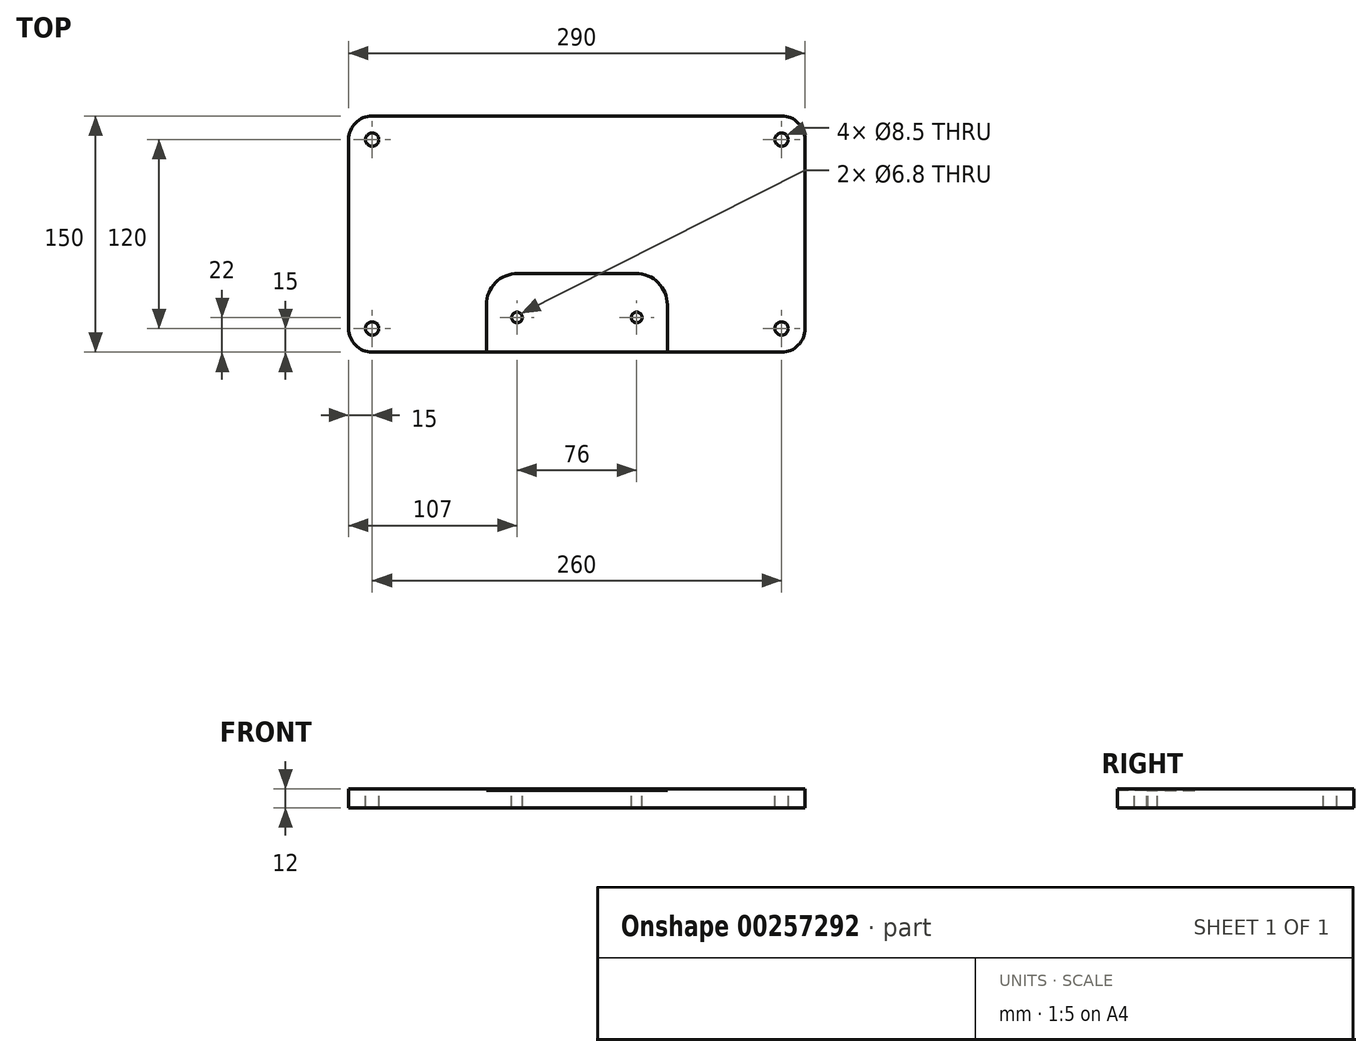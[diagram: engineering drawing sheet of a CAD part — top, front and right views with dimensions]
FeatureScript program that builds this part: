
annotation { "Feature Type Name" : "Feature", "Feature Type Description" : "" }
export const myFeature = defineFeature(function(context is Context, id is Id, definition is map)
    precondition{}
    {
        {
            var Q0;
            Q0=qCreatedBy(makeId("Top.planeOp"),FACE);
            var sketch = newSketch(context, id + "F0", { "sketchPlane" : qUnion([Q0])});
            skLineSegment(sketch, "E0", {"start": v(145, 150) * mm, "end": v(145, 0) * mm});
            skLineSegment(sketch, "E1", {"start": v(145, 150) * mm, "end": v(-145, 150) * mm});
            skLineSegment(sketch, "E2.MirrorCS", {"start": v(-145, 150) * mm, "end": v(-145, 0) * mm});
            skLineSegment(sketch, "E3", {"start": v(-145, 0) * mm, "end": v(145, 0) * mm});
            skSolve(sketch);
        }
        {
            var Q0;
            Q0=makeQuery(id+"F0.imprint","IMPRINT",FACE,{"disambiguationData":[TD([[makeQuery(id+"F0.imprint","IMPRINT",EDGE,{"derivedFrom":sQuery(id+"F0.wireOp",EDGE,"E0")}),-1.0]])]});
            extrude(context, id + "F1", {"entities" : qUnion([Q0]), "oppositeDirection" : true, "depth" : 12 * mm});
        }
        {
            var Q0;
            Q0=makeQuery(id+"F1.opExtrude","SWEPT_EDGE",EDGE,{"disambiguationData":[OSD([sQuery(id+"F0.wireOp",EDGE,"E1"),sQuery(id+"F0.wireOp",EDGE,"E2.MirrorCS")])]});
            var Q1;
            Q1=makeQuery(id+"F1.opExtrude","SWEPT_EDGE",EDGE,{"disambiguationData":[OSD([sQuery(id+"F0.wireOp",EDGE,"E2.MirrorCS"),sQuery(id+"F0.wireOp",EDGE,"E3")])]});
            var Q2;
            Q2=makeQuery(id+"F1.opExtrude","SWEPT_EDGE",EDGE,{"disambiguationData":[OSD([sQuery(id+"F0.wireOp",EDGE,"E0"),sQuery(id+"F0.wireOp",EDGE,"E1")])]});
            var Q3;
            Q3=makeQuery(id+"F1.opExtrude","SWEPT_EDGE",EDGE,{"disambiguationData":[OSD([sQuery(id+"F0.wireOp",EDGE,"E0"),sQuery(id+"F0.wireOp",EDGE,"E3")])]});
            fillet(context, id + "F2", {"entities" : qUnion([Q0, Q1, Q2, Q3]), "radius" : 15 * mm, "tangentPropagation" : true, "allowEdgeOverflow" : false});
        }
        {
            var Q0;
            Q0=makeQuery(id+"F1.opExtrude","CAP_FACE",FACE,{"disambiguationData":[OSD([sQuery(id+"F0.wireOp",EDGE,"E0"),sQuery(id+"F0.wireOp",EDGE,"E1"),sQuery(id+"F0.wireOp",EDGE,"E2.MirrorCS"),sQuery(id+"F0.wireOp",EDGE,"E3")])],"isStart":true});
            var sketch = newSketch(context, id + "F3", { "sketchPlane" : qUnion([Q0])});
            skPoint(sketch, "E4", {"position": v(130, 135) * mm});
            skPoint(sketch, "E5", {"position": v(130, 15) * mm});
            skPoint(sketch, "E6.MirrorP", {"position": v(-130, 135) * mm});
            skPoint(sketch, "E7.MirrorP", {"position": v(-130, 15) * mm});
            skLineSegment(sketch, "E8", {"start": v(57.5, 30) * mm, "end": v(57.5, -8) * mm});
            skLineSegment(sketch, "E9.MirrorCS", {"start": v(-57.5, 30) * mm, "end": v(-57.5, -8) * mm});
            skLineSegment(sketch, "E10", {"start": v(-37.5, 50) * mm, "end": v(37.5, 50) * mm});
            skLineSegment(sketch, "E11", {"start": v(-57.5, -8) * mm, "end": v(57.5, -8) * mm});
            skPoint(sketch, "E12.visualSharp", {"position": v(-57.5, 50) * mm});
            skArc(sketch, "E12.filletArc", {"start": v(-37.5, 50) * mm, "mid": v(-51.64, 44.14) * mm, "end": v(-57.5, 30) * mm});
            skPoint(sketch, "E13.visualSharp", {"position": v(57.5, 50) * mm});
            skArc(sketch, "E13.filletArc", {"start": v(57.5, 30) * mm, "mid": v(51.64, 44.14) * mm, "end": v(37.5, 50) * mm});
            skLineSegment(sketch, "E14", {"start": v(-47.11, 22) * mm, "end": v(45.69, 22) * mm, "construction": true});
            skPoint(sketch, "E15", {"position": v(38, 22) * mm});
            skPoint(sketch, "E16.MirrorP", {"position": v(-38, 22) * mm});
            skSolve(sketch);
        }
        {
            var Q0;
            Q0=sQuery(id+"F3.wireOp",VERTEX,"E4");
            var Q1;
            Q1=sQuery(id+"F3.wireOp",VERTEX,"E5");
            var Q2;
            Q2=sQuery(id+"F3.wireOp",VERTEX,"E6.MirrorP");
            var Q3;
            Q3=sQuery(id+"F3.wireOp",VERTEX,"E7.MirrorP");
            var Q4;
            Q4=makeQuery(id+"F1.opExtrude","SWEPT_BODY",BODY,{"disambiguationData":[OSD([sQuery(id+"F0.wireOp",EDGE,"E0"),sQuery(id+"F0.wireOp",EDGE,"E1"),sQuery(id+"F0.wireOp",EDGE,"E2.MirrorCS"),sQuery(id+"F0.wireOp",EDGE,"E3")])]});
            hole(context, id + "F4", {"style" : HoleStyle.SIMPLE, "endStyle" : HoleEndStyle.THROUGH, "standardTappedOrClearance" : lookupTablePath({ "standard" : "ISO", "fit" : "Normal", "engagement" : "75%", "pitch" : "1.5 mm", "size" : "M10", "type" : "Tapped" }), "standardBlindInLast" : lookupTablePath({ "fit" : "Standard", "standard" : "ISO", "engagement" : "75%", "pitch" : "1.5 mm", "size" : "M10", "type" : "Tapped" }), "holeDiameter" : 8.5 * mm, "showTappedDepth" : true, "tappedDepth" : 12 * mm, "tapClearance" : 3, "locations" : qUnion([Q0, Q1, Q2, Q3]), "scope" : qUnion([Q4]), "majorDiameter" : 10 * mm});
        }
        {
            var Q0;
            {var subQ0=sQuery(id+"F3.wireOp",EDGE,"E11");Q0=makeQuery(id+"F3.imprint","IMPRINT",FACE,{"disambiguationData":[TD([[makeQuery(id+"F3.imprint","IMPRINT",EDGE,{"derivedFrom":subQ0}),1.0]])]});}
            var Q1;
            Q1=makeQuery(id+"F3.imprint","IMPRINT",FACE,{"disambiguationData":[TD([[makeQuery(id+"F3.imprint","IMPRINT",EDGE,{"derivedFrom":sQuery(id+"F3.wireOp",EDGE,"E10")}),-1.0]])]});
            extrude(context, id + "F5", {"entities" : qUnion([Q0, Q1]), "operationType" : NewBodyOperationType.REMOVE, "oppositeDirection" : true, "depth" : 1 * mm});
        }
        {
            var Q0;
            Q0=sQuery(id+"F3.wireOp",VERTEX,"E15");
            var Q1;
            Q1=sQuery(id+"F3.wireOp",VERTEX,"E16.MirrorP");
            var Q2;
            Q2=makeQuery(id+"F1.opExtrude","SWEPT_BODY",BODY,{"disambiguationData":[OSD([sQuery(id+"F0.wireOp",EDGE,"E0"),sQuery(id+"F0.wireOp",EDGE,"E1"),sQuery(id+"F0.wireOp",EDGE,"E2.MirrorCS"),sQuery(id+"F0.wireOp",EDGE,"E3")])]});
            hole(context, id + "F6", {"style" : HoleStyle.SIMPLE, "endStyle" : HoleEndStyle.THROUGH, "standardTappedOrClearance" : lookupTablePath({ "standard" : "ISO", "fit" : "Normal", "engagement" : "75%", "pitch" : "1.25 mm", "size" : "M8", "type" : "Tapped" }), "standardBlindInLast" : lookupTablePath({ "fit" : "Standard", "standard" : "ISO", "engagement" : "75%", "pitch" : "1.25 mm", "size" : "M8", "type" : "Tapped" }), "holeDiameter" : 6.8 * mm, "showTappedDepth" : true, "tappedDepth" : 12 * mm, "tapClearance" : 3, "locations" : qUnion([Q0, Q1]), "scope" : qUnion([Q2]), "majorDiameter" : 8 * mm});
        }
    });
